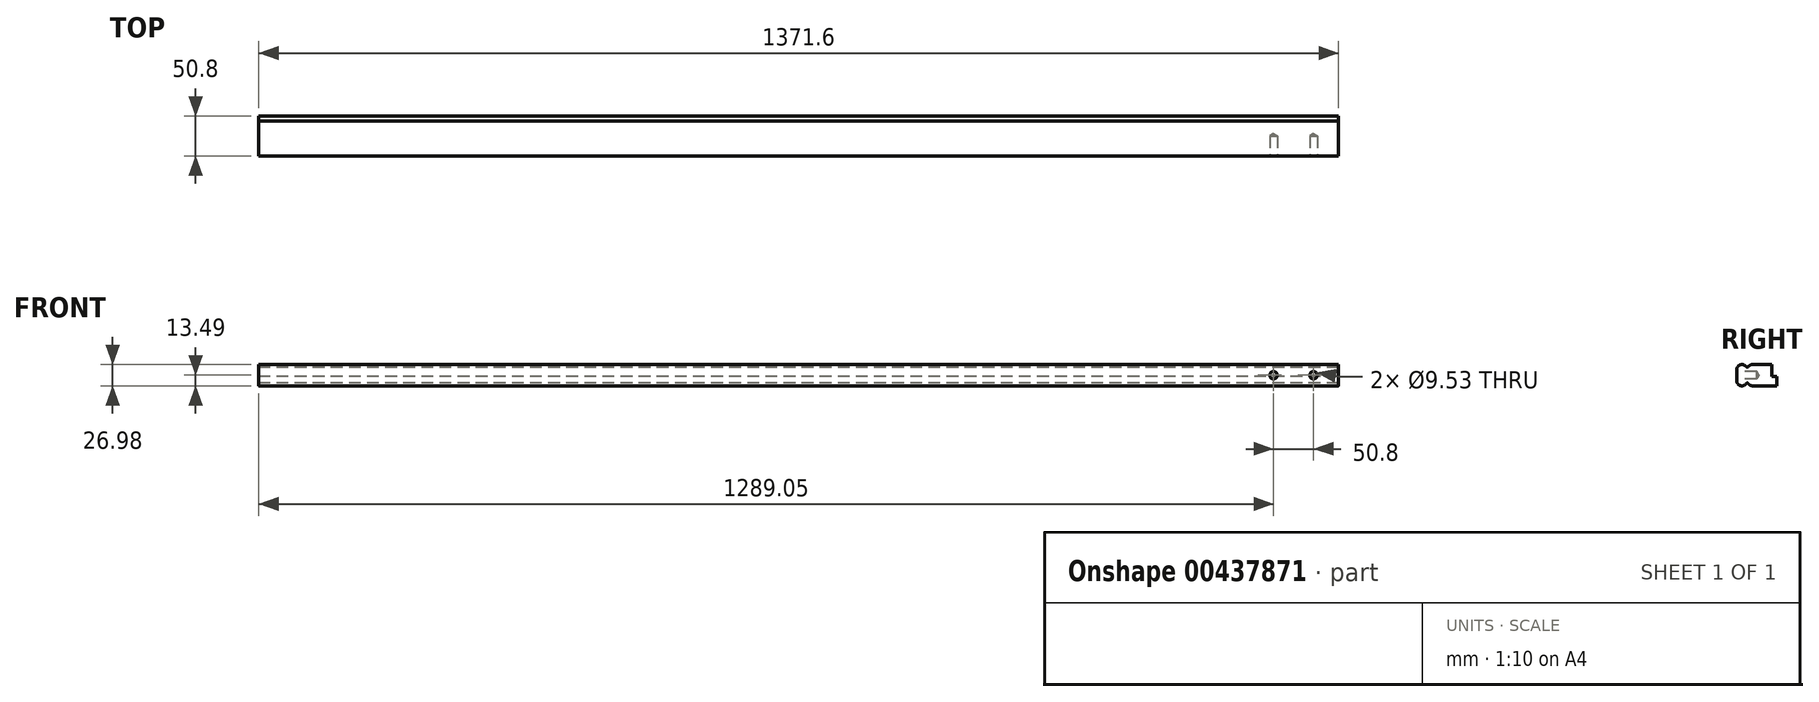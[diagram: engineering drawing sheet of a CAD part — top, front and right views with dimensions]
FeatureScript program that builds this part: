
annotation { "Feature Type Name" : "Feature", "Feature Type Description" : "" }
export const myFeature = defineFeature(function(context is Context, id is Id, definition is map)
    precondition{}
    {
        {
            var Q0;
            Q0=qCreatedBy(makeId("Right.planeOp"),FACE);
            var sketch = newSketch(context, id + "F0", { "sketchPlane" : qUnion([Q0])});
            skLineSegment(sketch, "E0.bottom", {"start": v(19.05, 13.5) * mm, "end": v(-5.16, 13.5) * mm});
            skLineSegment(sketch, "E0.right", {"start": v(-25.4, 6.75) * mm, "end": v(-25.4, -6.75) * mm});
            skArc(sketch, "E1", {"start": v(-13.26, 10.8) * mm, "mid": v(-20.79, 13.15) * mm, "end": v(-25.4, 6.75) * mm});
            skPoint(sketch, "E1.first.point", {"position": v(-25.4, 6.75) * mm});
            skPoint(sketch, "E1.second.point", {"position": v(-18.65, 13.5) * mm});
            skPoint(sketch, "E1.third.point", {"position": v(-18.65, 0) * mm});
            skArc(sketch, "E2", {"start": v(-5.16, 13.5) * mm, "mid": v(-8.18, 12.78) * mm, "end": v(-10.56, 10.8) * mm});
            skPoint(sketch, "E2.first.point", {"position": v(-11.9, 6.75) * mm});
            skPoint(sketch, "E2.second.point", {"position": v(-5.16, 0) * mm});
            skPoint(sketch, "E2.third.point", {"position": v(-5.16, 13.5) * mm});
            skArc(sketch, "E3", {"start": v(-13.26, 10.8) * mm, "mid": v(-11.9, 10.12) * mm, "end": v(-10.56, 10.8) * mm});
            skPoint(sketch, "E3.first.point", {"position": v(-13.26, 10.8) * mm});
            skPoint(sketch, "E3.second.point", {"position": v(-10.56, 10.8) * mm});
            skPoint(sketch, "E3.third.point", {"position": v(-11.9, 13.5) * mm});
            skArc(sketch, "E4.MirrorCS", {"start": v(-13.26, -10.8) * mm, "mid": v(-11.9, -10.12) * mm, "end": v(-10.56, -10.8) * mm});
            skPoint(sketch, "E5.MirrorP", {"position": v(-10.56, -10.8) * mm});
            skPoint(sketch, "E6.MirrorP", {"position": v(-25.4, -6.75) * mm});
            skPoint(sketch, "E7.MirrorP", {"position": v(-13.26, -10.8) * mm});
            skArc(sketch, "E8.MirrorCS", {"start": v(-13.26, -10.8) * mm, "mid": v(-20.79, -13.15) * mm, "end": v(-25.4, -6.75) * mm});
            skPoint(sketch, "E9.MirrorP", {"position": v(-11.9, -13.5) * mm});
            skArc(sketch, "E10.MirrorCS", {"start": v(-5.16, -13.5) * mm, "mid": v(-8.18, -12.78) * mm, "end": v(-10.56, -10.8) * mm});
            skPoint(sketch, "E11.MirrorP", {"position": v(-5.16, -13.5) * mm});
            skPoint(sketch, "E12.MirrorP", {"position": v(-11.9, -6.75) * mm});
            skPoint(sketch, "E13.MirrorP", {"position": v(-18.65, -13.5) * mm});
            skLineSegment(sketch, "E14.MirrorCS", {"start": v(25.4, -13.5) * mm, "end": v(-5.16, -13.5) * mm});
            skLineSegment(sketch, "E15", {"start": v(25.4, -1.59) * mm, "end": v(25.4, -13.5) * mm});
            skLineSegment(sketch, "E16.top", {"start": v(25.4, -1.59) * mm, "end": v(19.05, -1.59) * mm});
            skLineSegment(sketch, "E16.right", {"start": v(19.05, 13.5) * mm, "end": v(19.05, -1.59) * mm});
            skPoint(sketch, "E17.orphan", {"position": v(25.4, 13.5) * mm});
            skSolve(sketch);
        }
        {
            var Q0;
            Q0=qSketchRegion(id+"F0",true);
            extrude(context, id + "F1", {"entities" : qUnion([Q0]), "depth" : 1371.6 * mm, "symmetric" : true});
        }
        {
            var Q0;
            Q0=makeQuery(id+"F1.opExtrude","SWEPT_FACE",FACE,{"disambiguationData":[OSD([sQuery(id+"F0.wireOp",EDGE,"E0.right")])]});
            var sketch = newSketch(context, id + "F2", { "sketchPlane" : qUnion([Q0])});
            skPoint(sketch, "E18", {"position": v(654.05, 0) * mm});
            skPoint(sketch, "E19", {"position": v(603.25, 0) * mm});
            skSolve(sketch);
        }
        {
            var Q0;
            Q0=sQuery(id+"F2.wireOp",VERTEX,"E18");
            var Q1;
            Q1=sQuery(id+"F2.wireOp",VERTEX,"E19");
            var Q2;
            Q2=makeQuery(id+"F1.opExtrude","SWEPT_BODY",BODY,{"disambiguationData":[OSD([sQuery(id+"F0.wireOp",EDGE,"E0.bottom"),sQuery(id+"F0.wireOp",EDGE,"E0.right"),sQuery(id+"F0.wireOp",EDGE,"E1"),sQuery(id+"F0.wireOp",EDGE,"E2"),sQuery(id+"F0.wireOp",EDGE,"E3"),sQuery(id+"F0.wireOp",EDGE,"E4.MirrorCS"),sQuery(id+"F0.wireOp",EDGE,"E8.MirrorCS"),sQuery(id+"F0.wireOp",EDGE,"E10.MirrorCS"),sQuery(id+"F0.wireOp",EDGE,"E14.MirrorCS"),sQuery(id+"F0.wireOp",EDGE,"E15"),sQuery(id+"F0.wireOp",EDGE,"E16.top"),sQuery(id+"F0.wireOp",EDGE,"E16.right")])]});
            hole(context, id + "F3", {"style" : HoleStyle.SIMPLE, "endStyle" : HoleEndStyle.BLIND, "holeDiameter" : 9.52 * mm, "holeDepth" : 25.4 * mm, "isTappedThrough" : true, "tappedDepth" : 12.7 * mm, "tapClearance" : 3, "locations" : qUnion([Q0, Q1]), "scope" : qUnion([Q2])});
        }
    });
